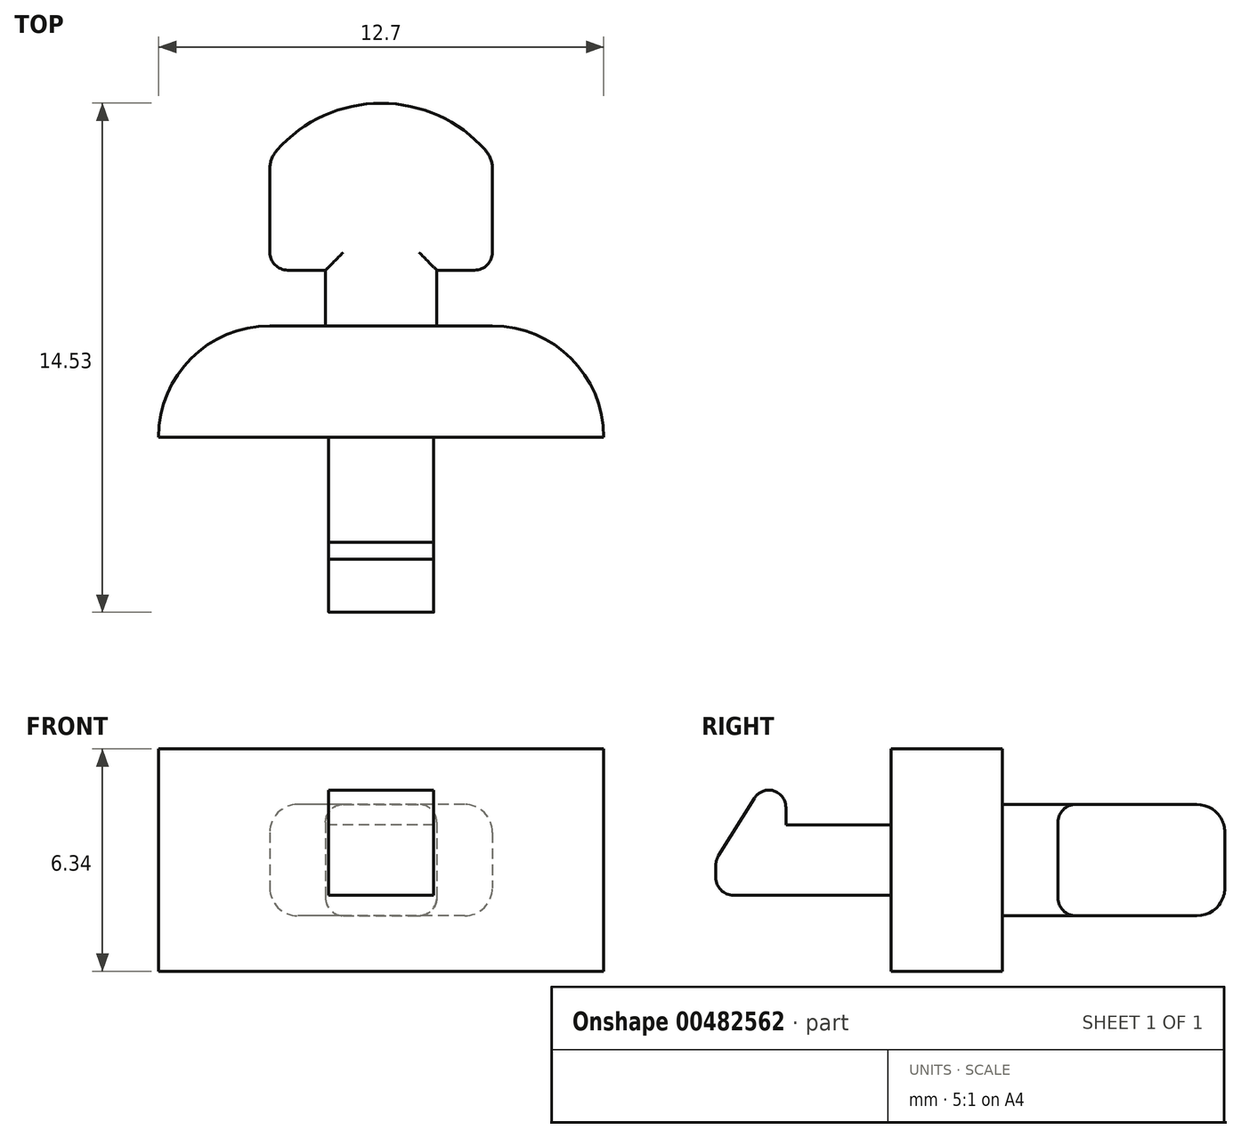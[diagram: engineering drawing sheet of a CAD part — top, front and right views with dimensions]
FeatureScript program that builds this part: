
annotation { "Feature Type Name" : "Feature", "Feature Type Description" : "" }
export const myFeature = defineFeature(function(context is Context, id is Id, definition is map)
    precondition{}
    {
        {
            var Q0;
            Q0=qCreatedBy(makeId("Top.planeOp"),FACE);
            var sketch = newSketch(context, id + "F0", { "sketchPlane" : qUnion([Q0])});
            skLineSegment(sketch, "E0", {"start": v(3.18, 7.94) * mm, "end": v(3.18, 4.76) * mm});
            skLineSegment(sketch, "E1", {"start": v(3.18, 4.76) * mm, "end": v(1.59, 4.76) * mm});
            skLineSegment(sketch, "E2", {"start": v(1.59, 4.76) * mm, "end": v(1.59, 3.17) * mm});
            skLineSegment(sketch, "E3", {"start": v(-1.59, 3.17) * mm, "end": v(-1.59, 4.76) * mm});
            skLineSegment(sketch, "E4", {"start": v(-1.59, 4.76) * mm, "end": v(-3.17, 4.76) * mm});
            skLineSegment(sketch, "E5", {"start": v(-3.17, 4.76) * mm, "end": v(-3.17, 7.94) * mm});
            skLineSegment(sketch, "E6", {"start": v(0, 34.93) * mm, "end": v(0, -21.9) * mm, "construction": true});
            skArc(sketch, "E7", {"start": v(3.18, 7.94) * mm, "mid": v(0, 9.52) * mm, "end": v(-3.17, 7.94) * mm});
            skLineSegment(sketch, "E8", {"start": v(1.59, 3.18) * mm, "end": v(6.35, 3.18) * mm});
            skLineSegment(sketch, "E9", {"start": v(6.35, 3.18) * mm, "end": v(6.35, 0) * mm});
            skLineSegment(sketch, "E10", {"start": v(6.35, 0) * mm, "end": v(-6.35, 0) * mm});
            skLineSegment(sketch, "E11", {"start": v(-6.35, 0) * mm, "end": v(-6.35, 3.17) * mm});
            skLineSegment(sketch, "E12", {"start": v(-6.35, 3.17) * mm, "end": v(-1.59, 3.17) * mm});
            skLineSegment(sketch, "E13", {"start": v(-6.75, 9.52) * mm, "end": v(5.45, 9.52) * mm, "construction": true});
            skLineSegment(sketch, "E14", {"start": v(-1.59, 3.17) * mm, "end": v(1.59, 3.17) * mm});
            skSolve(sketch);
        }
        {
            var Q0;
            Q0=makeQuery(id+"F0.imprint","IMPRINT",FACE,{"disambiguationData":[TD([[makeQuery(id+"F0.imprint","IMPRINT",EDGE,{"derivedFrom":sQuery(id+"F0.wireOp",EDGE,"E0")}),-1.0]])]});
            extrude(context, id + "F1", {"entities" : qUnion([Q0]), "endBound" : BoundingType.SYMMETRIC, "depth" : 3.17 * mm});
        }
        {
            var Q0;
            Q0=makeQuery(id+"F0.imprint","IMPRINT",FACE,{"disambiguationData":[TD([[makeQuery(id+"F0.imprint","IMPRINT",EDGE,{"derivedFrom":sQuery(id+"F0.wireOp",EDGE,"E8")}),-1.0]])]});
            extrude(context, id + "F2", {"entities" : qUnion([Q0]), "operationType" : NewBodyOperationType.ADD, "endBound" : BoundingType.SYMMETRIC, "depth" : 6.35 * mm});
        }
        {
            var Q0;
            Q0=makeQuery(id+"F2.opExtrude","SWEPT_EDGE",EDGE,{"disambiguationData":[OSD([sQuery(id+"F0.wireOp",EDGE,"E8"),sQuery(id+"F0.wireOp",EDGE,"E9")])]});
            var Q1;
            Q1=makeQuery(id+"F2.opExtrude","SWEPT_EDGE",EDGE,{"disambiguationData":[OSD([sQuery(id+"F0.wireOp",EDGE,"E11"),sQuery(id+"F0.wireOp",EDGE,"E12")])]});
            fillet(context, id + "F3", {"entities" : qUnion([Q0, Q1]), "radius" : 3.17 * mm, "tangentPropagation" : true, "allowEdgeOverflow" : false});
        }
        {
            var Q0;
            Q0=makeQuery(id+"F1.opExtrude","CAP_EDGE",EDGE,{"disambiguationData":[OSD([sQuery(id+"F0.wireOp",EDGE,"E7")])],"isStart":true});
            var Q1;
            Q1=makeQuery(id+"F1.opExtrude","CAP_EDGE",EDGE,{"disambiguationData":[OSD([sQuery(id+"F0.wireOp",EDGE,"E7")])],"isStart":false});
            var Q2;
            Q2=makeQuery(id+"F1.opExtrude","CAP_EDGE",EDGE,{"disambiguationData":[OSD([sQuery(id+"F0.wireOp",EDGE,"E0")])],"isStart":true});
            var Q3;
            Q3=makeQuery(id+"F1.opExtrude","CAP_EDGE",EDGE,{"disambiguationData":[OSD([sQuery(id+"F0.wireOp",EDGE,"E0")])],"isStart":false});
            var Q4;
            Q4=makeQuery(id+"F1.opExtrude","CAP_EDGE",EDGE,{"disambiguationData":[OSD([sQuery(id+"F0.wireOp",EDGE,"E5")])],"isStart":true});
            var Q5;
            Q5=makeQuery(id+"F1.opExtrude","CAP_EDGE",EDGE,{"disambiguationData":[OSD([sQuery(id+"F0.wireOp",EDGE,"E5")])],"isStart":false});
            var Q6;
            Q6=makeQuery(id+"F1.opExtrude","SWEPT_EDGE",EDGE,{"disambiguationData":[OSD([sQuery(id+"F0.wireOp",EDGE,"E0"),sQuery(id+"F0.wireOp",EDGE,"E7")])]});
            var Q7;
            Q7=makeQuery(id+"F1.opExtrude","SWEPT_EDGE",EDGE,{"disambiguationData":[OSD([sQuery(id+"F0.wireOp",EDGE,"E5"),sQuery(id+"F0.wireOp",EDGE,"E7")])]});
            fillet(context, id + "F4", {"entities" : qUnion([Q0, Q1, Q2, Q3, Q4, Q5, Q6, Q7]), "radius" : 0.8 * mm, "tangentPropagation" : true, "allowEdgeOverflow" : false});
        }
        {
            var Q0;
            Q0=makeQuery(id+"F1.opExtrude","CAP_EDGE",EDGE,{"disambiguationData":[OSD([sQuery(id+"F0.wireOp",EDGE,"E14")])],"isStart":true});
            var Q1;
            Q1=makeQuery(id+"F1.opExtrude","SWEPT_EDGE",EDGE,{"disambiguationData":[OSD([sQuery(id+"F0.wireOp",EDGE,"E3"),sQuery(id+"F0.wireOp",EDGE,"E12"),sQuery(id+"F0.wireOp",EDGE,"E14")])]});
            var Q2;
            Q2=makeQuery(id+"F1.opExtrude","CAP_EDGE",EDGE,{"disambiguationData":[OSD([sQuery(id+"F0.wireOp",EDGE,"E14")])],"isStart":false});
            var Q3;
            Q3=makeQuery(id+"F1.opExtrude","SWEPT_EDGE",EDGE,{"disambiguationData":[OSD([sQuery(id+"F0.wireOp",EDGE,"E2"),sQuery(id+"F0.wireOp",EDGE,"E8"),sQuery(id+"F0.wireOp",EDGE,"E14")])]});
            var Q4;
            Q4=makeQuery(id+"F1.opExtrude","CAP_EDGE",EDGE,{"disambiguationData":[OSD([sQuery(id+"F0.wireOp",EDGE,"E2")])],"isStart":false});
            var Q5;
            Q5=makeQuery(id+"F1.opExtrude","CAP_EDGE",EDGE,{"disambiguationData":[OSD([sQuery(id+"F0.wireOp",EDGE,"E2")])],"isStart":true});
            var Q6;
            Q6=makeQuery(id+"F1.opExtrude","CAP_EDGE",EDGE,{"disambiguationData":[OSD([sQuery(id+"F0.wireOp",EDGE,"E3")])],"isStart":true});
            var Q7;
            Q7=makeQuery(id+"F1.opExtrude","CAP_EDGE",EDGE,{"disambiguationData":[OSD([sQuery(id+"F0.wireOp",EDGE,"E3")])],"isStart":false});
            var Q8;
            Q8=makeQuery(id+"F4.opFillet","BLEND_EDGE",EDGE,{"blendedFrom":[makeQuery(id+"F1.opExtrude","CAP_EDGE",EDGE,{"disambiguationData":[OSD([sQuery(id+"F0.wireOp",EDGE,"E0")])],"isStart":false}),makeQuery(id+"F1.opExtrude","SWEPT_FACE",FACE,{"disambiguationData":[OSD([sQuery(id+"F0.wireOp",EDGE,"E1")])]})],"blendedInto":[makeQuery(id+"F1.opExtrude","SWEPT_FACE",FACE,{"disambiguationData":[OSD([sQuery(id+"F0.wireOp",EDGE,"E1")])]})]});
            var Q9;
            Q9=makeQuery(id+"F4.opFillet","BLEND_EDGE",EDGE,{"blendedFrom":[makeQuery(id+"F1.opExtrude","CAP_EDGE",EDGE,{"disambiguationData":[OSD([sQuery(id+"F0.wireOp",EDGE,"E5")])],"isStart":true}),makeQuery(id+"F1.opExtrude","SWEPT_FACE",FACE,{"disambiguationData":[OSD([sQuery(id+"F0.wireOp",EDGE,"E4")])]})],"blendedInto":[makeQuery(id+"F1.opExtrude","SWEPT_FACE",FACE,{"disambiguationData":[OSD([sQuery(id+"F0.wireOp",EDGE,"E4")])]})]});
            fillet(context, id + "F5", {"entities" : qUnion([Q0, Q1, Q2, Q3, Q4, Q5, Q6, Q7, Q8, Q9]), "radius" : 0.5 * mm, "tangentPropagation" : true, "allowEdgeOverflow" : false});
        }
        {
            var Q0;
            Q0=qCreatedBy(makeId("Right.planeOp"),FACE);
            var sketch = newSketch(context, id + "F6", { "sketchPlane" : qUnion([Q0])});
            skLineSegment(sketch, "E15", {"start": v(0, 1) * mm, "end": v(-3, 1) * mm});
            skLineSegment(sketch, "E16", {"start": v(-3, 1) * mm, "end": v(-3, 2) * mm});
            skLineSegment(sketch, "E17", {"start": v(-3, 2) * mm, "end": v(-3.75, 2) * mm});
            skLineSegment(sketch, "E18", {"start": v(-5, -1) * mm, "end": v(0, -1) * mm});
            skLineSegment(sketch, "E19", {"start": v(0, -1) * mm, "end": v(0, 1) * mm});
            skLineSegment(sketch, "E20", {"start": v(0, 0) * mm, "end": v(-4, 0) * mm, "construction": true});
            skLineSegment(sketch, "E21", {"start": v(-4, 0) * mm, "end": v(-4, 4.54) * mm, "construction": true});
            skLineSegment(sketch, "E22", {"start": v(-3.75, 2) * mm, "end": v(-5, 0) * mm});
            skLineSegment(sketch, "E23", {"start": v(-5, 0) * mm, "end": v(-5, -1) * mm});
            skSolve(sketch);
        }
        {
            var Q0;
            Q0=makeQuery(id+"F6.imprint","IMPRINT",FACE,{"disambiguationData":[TD([[makeQuery(id+"F6.imprint","IMPRINT",EDGE,{"derivedFrom":sQuery(id+"F6.wireOp",EDGE,"E15")}),1.0]])]});
            extrude(context, id + "F7", {"entities" : qUnion([Q0]), "operationType" : NewBodyOperationType.ADD, "endBound" : BoundingType.SYMMETRIC, "depth" : 3 * mm, "offsetDistance" : 25.4 * mm});
        }
        {
            var Q0;
            Q0=makeQuery(id+"F7.opExtrude","SWEPT_EDGE",EDGE,{"disambiguationData":[OSD([sQuery(id+"F6.wireOp",EDGE,"E18"),sQuery(id+"F6.wireOp",EDGE,"E23")])]});
            var Q1;
            Q1=makeQuery(id+"F7.opExtrude","SWEPT_EDGE",EDGE,{"disambiguationData":[OSD([sQuery(id+"F6.wireOp",EDGE,"E22"),sQuery(id+"F6.wireOp",EDGE,"E23")])]});
            var Q2;
            Q2=makeQuery(id+"F7.opExtrude","SWEPT_EDGE",EDGE,{"disambiguationData":[OSD([sQuery(id+"F6.wireOp",EDGE,"E17"),sQuery(id+"F6.wireOp",EDGE,"E22")])]});
            var Q3;
            Q3=makeQuery(id+"F7.opExtrude","SWEPT_EDGE",EDGE,{"disambiguationData":[OSD([sQuery(id+"F6.wireOp",EDGE,"E16"),sQuery(id+"F6.wireOp",EDGE,"E17")])]});
            fillet(context, id + "F8", {"entities" : qUnion([Q0, Q1, Q2, Q3]), "radius" : .5 * mm, "tangentPropagation" : true, "allowEdgeOverflow" : false});
        }
    });
